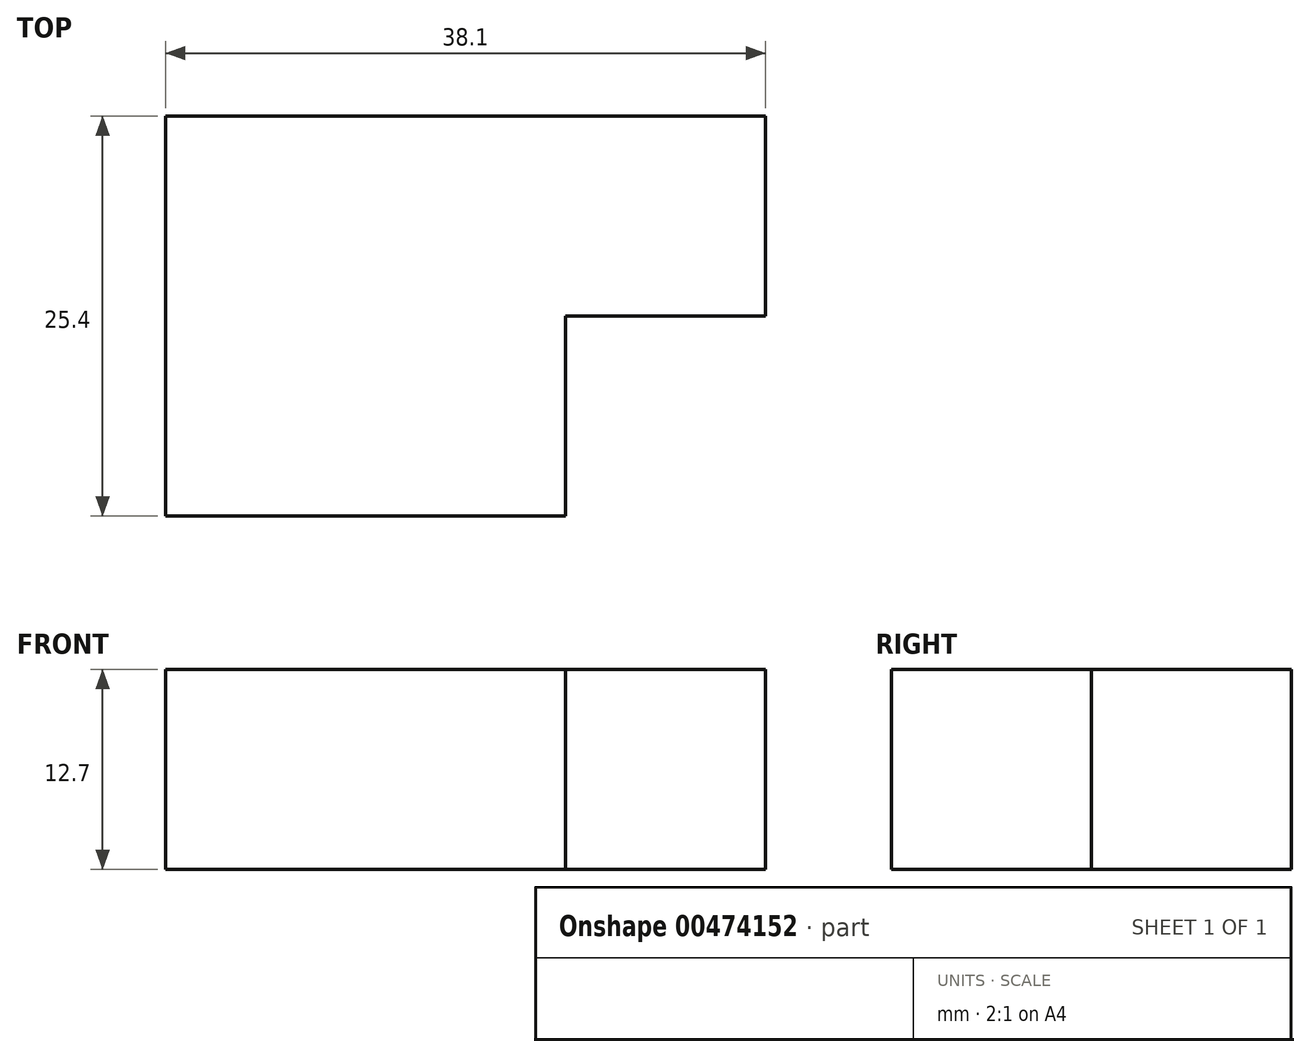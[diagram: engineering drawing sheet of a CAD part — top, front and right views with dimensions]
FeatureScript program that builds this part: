
annotation { "Feature Type Name" : "Feature", "Feature Type Description" : "" }
export const myFeature = defineFeature(function(context is Context, id is Id, definition is map)
    precondition{}
    {
        {
            var Q0;
            Q0=qCreatedBy(makeId("Top.planeOp"),FACE);
            var sketch = newSketch(context, id + "F0", { "sketchPlane" : qUnion([Q0])});
            skLineSegment(sketch, "E0", {"start": v(-18.16, 16.4) * mm, "end": v(19.94, 16.4) * mm});
            skLineSegment(sketch, "E1", {"start": v(19.94, 16.4) * mm, "end": v(19.94, 3.7) * mm});
            skLineSegment(sketch, "E2", {"start": v(19.94, 3.7) * mm, "end": v(7.24, 3.7) * mm});
            skLineSegment(sketch, "E3", {"start": v(7.24, 3.7) * mm, "end": v(7.24, -9) * mm});
            skLineSegment(sketch, "E4", {"start": v(7.24, -9) * mm, "end": v(-18.16, -9) * mm});
            skLineSegment(sketch, "E5", {"start": v(-18.16, -9) * mm, "end": v(-18.16, 16.4) * mm});
            skSolve(sketch);
        }
        {
            var Q0;
            Q0=makeQuery(id+"F0.imprint","IMPRINT",FACE,{"disambiguationData":[TD([[makeQuery(id+"F0.imprint","IMPRINT",EDGE,{"derivedFrom":sQuery(id+"F0.wireOp",EDGE,"E0")}),-1.0]])]});
            extrude(context, id + "F1", {"entities" : qUnion([Q0]), "depth" : 12.7 * mm});
        }
    });
